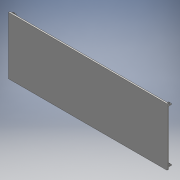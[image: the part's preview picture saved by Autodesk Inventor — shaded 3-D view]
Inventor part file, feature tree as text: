
AUTODESK INVENTOR PART (.ipt)
format: ipt  version: 2016 (Build 200138000, 138)  size: 129,536 bytes
history: native  units: mm
features: extrude x2, hole x2, sketch x2
ambient origin geometry x8: Origin, YZ Plane, XZ Plane, XY Plane, X Axis, Y Axis, Z Axis, Center Point
bodies: Solid1 (feature_tree)
feature tree (6):
  extrude  "Extrusion1"  Depth=65.0mm
  extrude  "Extrusion2"  Depth=59.5mm
  hole  "Hole1"  [1 undecoded]
  hole  "Hole2"  [1 undecoded]
  sketch  "Sketch1"  dims[d0=178.9mm d1=65.0mm]
  sketch  "Sketch2"  dims[d2=1.5mm d3=0.0mm d4=59.5mm d5=3.5mm d6=0.5mm d7=3.5mm d8=0.0mm d9=1.75mm d10=1.75mm d11=3.0mm d12=6.0mm d13=4.0mm d14=2.0mm d15=90.0deg d16=60.5mm d17=20.594885mm d18=1.75mm d19=1.75mm d20=3.0mm d21=6.0mm d22=4.0mm d23=2.0mm d24=90.0deg d25=60.5mm d26=20.594885mm]
note: 2 required parameter values undecoded (feature->parameter linkage not recoverable at this tier; creation-order binding heuristic only, values carry confidence <= 0.55)
